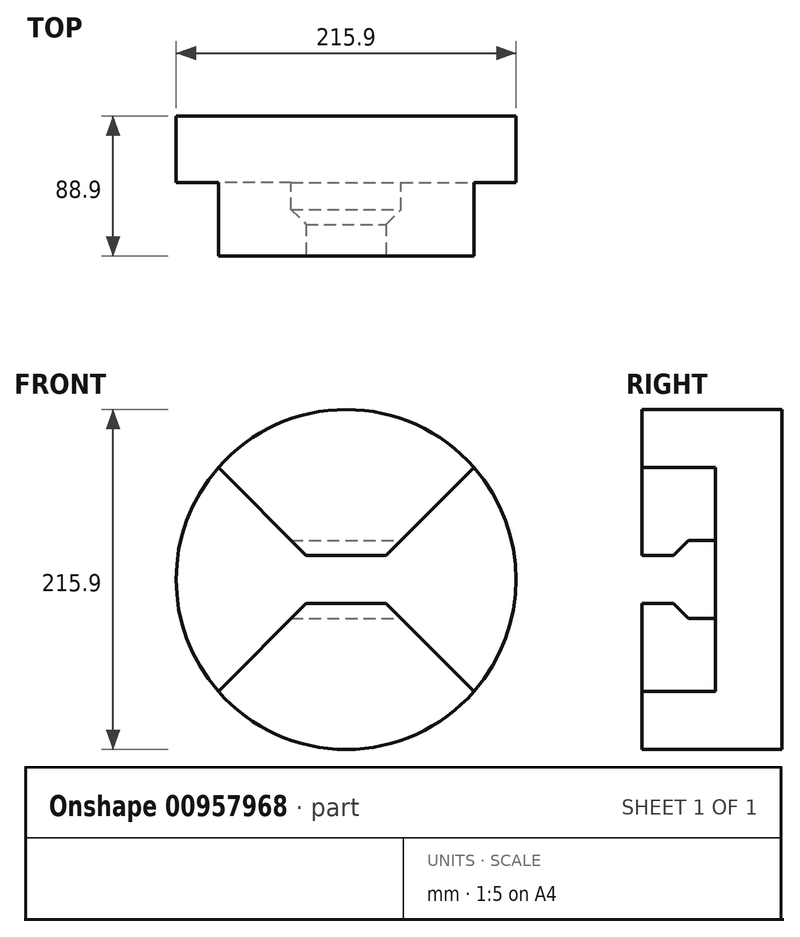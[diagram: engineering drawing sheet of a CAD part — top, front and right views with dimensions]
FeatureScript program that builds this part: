
annotation { "Feature Type Name" : "Feature", "Feature Type Description" : "" }
export const myFeature = defineFeature(function(context is Context, id is Id, definition is map)
    precondition{}
    {
        {
            var Q0;
            Q0=qCreatedBy(makeId("Front.planeOp"),FACE);
            var sketch = newSketch(context, id + "F0", { "sketchPlane" : qUnion([Q0])});
            skCircle(sketch, "E0", {"center": v(0, 0) * mm, "radius": 107.95 * mm});
            skSolve(sketch);
        }
        {
            var Q0;
            Q0 = qSketchRegion(id + "F0", true);
            extrude(context, id + "F1", {"entities" : qUnion([Q0]), "oppositeDirection" : true, "depth" : 88.9 * mm, "offsetDistance" : 25 * mm});
        }
        {
            var Q0;
            Q0=qCreatedBy(makeId("Front.planeOp"),FACE);
            var sketch = newSketch(context, id + "F2", { "sketchPlane" : qUnion([Q0])});
            skLineSegment(sketch, "E1", {"start": v(-25.4, 15.37) * mm, "end": v(-112.2, 102.17) * mm});
            skLineSegment(sketch, "E2", {"start": v(25.4, 15.37) * mm, "end": v(115.95, 105.92) * mm});
            skLineSegment(sketch, "E3", {"start": v(-25.4, -15.37) * mm, "end": v(-99.76, -89.72) * mm});
            skLineSegment(sketch, "E4", {"start": v(25.4, -15.37) * mm, "end": v(112.3, -102.26) * mm});
            skLineSegment(sketch, "E5", {"start": v(-112.2, 102.17) * mm, "end": v(-112.2, -81.35) * mm});
            skLineSegment(sketch, "E6", {"start": v(-112.2, -81.35) * mm, "end": v(-99.76, -89.72) * mm});
            skLineSegment(sketch, "E7", {"start": v(115.95, 105.92) * mm, "end": v(112.3, -102.26) * mm});
            skLineSegment(sketch, "E8.trimOffspring", {"start": v(-25.4, 15.37) * mm, "end": v(25.4, 15.37) * mm});
            skLineSegment(sketch, "E9.trimOffspring", {"start": v(-25.4, -15.37) * mm, "end": v(25.4, -15.37) * mm});
            skSolve(sketch);
        }
        {
            var Q0;
            Q0 = qSketchRegion(id + "F2", true);
            extrude(context, id + "F3", {"entities" : qUnion([Q0]), "operationType" : NewBodyOperationType.REMOVE, "oppositeDirection" : true, "depth" : 46.6 * mm, "offsetDistance" : 25 * mm});
        }
        {
            var Q0;
            Q0=qCreatedBy(makeId("Right.planeOp"),FACE);
            var sketch = newSketch(context, id + "F4", { "sketchPlane" : qUnion([Q0])});
            skLineSegment(sketch, "E10", {"start": v(29.6, 24.9) * mm, "end": v(46.6, 24.9) * mm});
            skLineSegment(sketch, "E11", {"start": v(46.6, 24.9) * mm, "end": v(46.6, -24.9) * mm});
            skLineSegment(sketch, "E12", {"start": v(46.6, -24.9) * mm, "end": v(29.6, -24.9) * mm});
            skLineSegment(sketch, "E13", {"start": v(29.6, -24.9) * mm, "end": v(20.07, -15.37) * mm});
            skLineSegment(sketch, "E14", {"start": v(29.6, 24.9) * mm, "end": v(20.07, 15.37) * mm});
            skLineSegment(sketch, "E15", {"start": v(20.07, 15.37) * mm, "end": v(-10.55, 15.37) * mm});
            skLineSegment(sketch, "E16", {"start": v(-10.55, 15.37) * mm, "end": v(-10.55, -15.02) * mm});
            skLineSegment(sketch, "E17", {"start": v(-10.55, -15.02) * mm, "end": v(20.07, -15.37) * mm});
            skSolve(sketch);
        }
        {
            var Q0;
            Q0 = qSketchRegion(id + "F4", true);
            extrude(context, id + "F5", {"entities" : qUnion([Q0]), "operationType" : NewBodyOperationType.REMOVE, "endBound" : BoundingType.SYMMETRIC, "oppositeDirection" : true, "depth" : 200 * mm, "offsetDistance" : 25 * mm});
        }
    });
